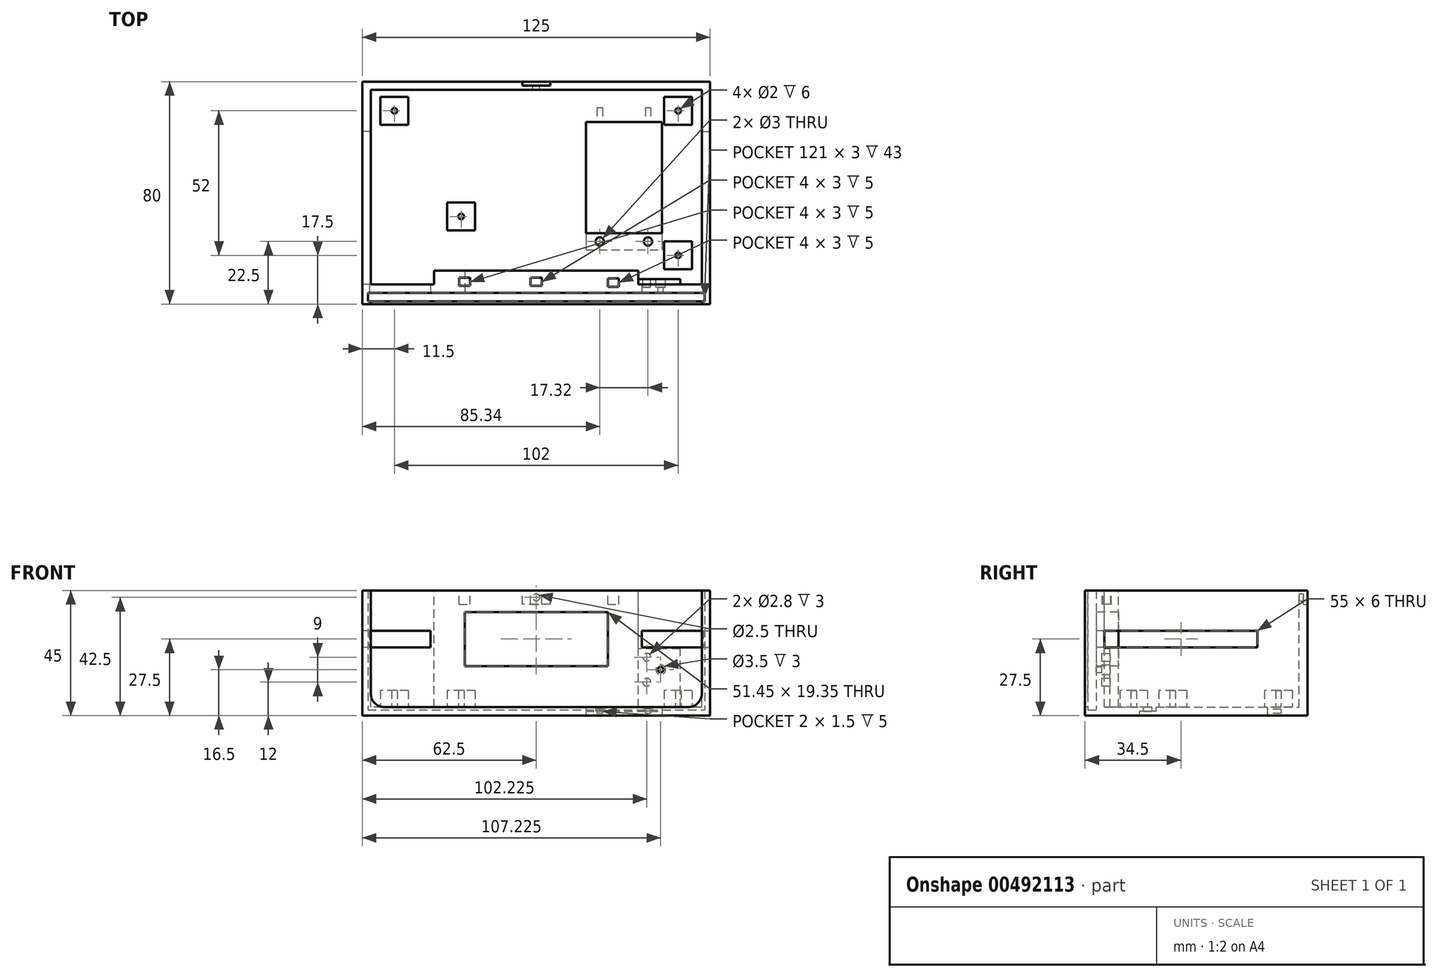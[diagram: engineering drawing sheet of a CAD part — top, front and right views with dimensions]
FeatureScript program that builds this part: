
annotation { "Feature Type Name" : "Feature", "Feature Type Description" : "" }
export const myFeature = defineFeature(function(context is Context, id is Id, definition is map)
    precondition{}
    {
        {
            var Q0;
            Q0=qCreatedBy(makeId("Top.planeOp"),FACE);
            var sketch = newSketch(context, id + "F0", { "sketchPlane" : qUnion([Q0])});
            skLineSegment(sketch, "E0.bottom", {"start": v(-62.5, 40) * mm, "end": v(62.5, 40) * mm});
            skLineSegment(sketch, "E0.top", {"start": v(-62.5, -40) * mm, "end": v(62.5, -40) * mm});
            skLineSegment(sketch, "E0.left", {"start": v(-62.5, 40) * mm, "end": v(-62.5, -40) * mm});
            skLineSegment(sketch, "E0.right", {"start": v(62.5, 40) * mm, "end": v(62.5, -40) * mm});
            skPoint(sketch, "E0.middle", {"position": v(0, 0) * mm});
            skSolve(sketch);
        }
        {
            var Q0;
            Q0 = qSketchRegion(id + "F0", true);
            var Q1;
            Q1 = qSketchRegion(id + "F2", true);
            extrude(context, id + "F1", {"entities" : qUnion([Q0, Q1]), "depth" : 45 * mm});
        }
        {
            var Q0;
            Q0=makeQuery(id+"F1.opExtrude","SWEPT_FACE",FACE,{"disambiguationData":[OSD([sQuery(id+"F0.wireOp",EDGE,"E0.top")])]});
            var sketch = newSketch(context, id + "F2", { "sketchPlane" : qUnion([Q0])});
            skArc(sketch, "E1", {"start": v(-59.5, 7.95) * mm, "mid": v(-58.05, 4.45) * mm, "end": v(-54.55, 3) * mm});
            skLineSegment(sketch, "E2", {"start": v(-59.5, 47) * mm, "end": v(-59.5, 7.95) * mm});
            skLineSegment(sketch, "E3", {"start": v(-54.55, 3) * mm, "end": v(0, 3) * mm});
            skLineSegment(sketch, "E4", {"start": v(0, 47) * mm, "end": v(-59.5, 47) * mm});
            skLineSegment(sketch, "E5.MirrorCS", {"start": v(0, 47) * mm, "end": v(59.5, 47) * mm});
            skLineSegment(sketch, "E6.MirrorCS", {"start": v(59.5, 47) * mm, "end": v(59.5, 7.95) * mm});
            skArc(sketch, "E7.MirrorCS", {"start": v(59.5, 7.95) * mm, "mid": v(58.05, 4.45) * mm, "end": v(54.55, 3) * mm});
            skLineSegment(sketch, "E8.MirrorCS", {"start": v(54.55, 3) * mm, "end": v(0, 3) * mm});
            skSolve(sketch);
        }
        {
            var Q0;
            Q0 = qSketchRegion(id + "F2", true);
            extrude(context, id + "F3", {"entities" : qUnion([Q0]), "operationType" : NewBodyOperationType.REMOVE, "oppositeDirection" : true, "depth" : 4 * mm});
        }
        {
            var Q0;
            Q0=makeQuery(id+"F3.boolean.opBoolean","COPY",FACE,{"derivedFrom":makeQuery(id+"F3.opExtrude","CAP_FACE",FACE,{"disambiguationData":[OSD([sQuery(id+"F2.wireOp",EDGE,"E1"),sQuery(id+"F2.wireOp",EDGE,"E2"),sQuery(id+"F2.wireOp",EDGE,"E3"),sQuery(id+"F2.wireOp",EDGE,"E4"),sQuery(id+"F2.wireOp",EDGE,"3b1f1dae-3a7a-4ead-be68-3ca8e11536510.MirrorCS"),sQuery(id+"F2.wireOp",EDGE,"84f603e4-86f5-4add-9121-f122701d1a8b0.MirrorCS"),sQuery(id+"F2.wireOp",EDGE,"d1928d76-ccfc-4052-b61b-d85eb2371b270.MirrorCS"),sQuery(id+"F2.wireOp",EDGE,"2d53626f-7717-42d7-a231-c828f44102550.MirrorCS")])],"isStart":false})});
            var sketch = newSketch(context, id + "F4", { "sketchPlane" : qUnion([Q0])});
            skLineSegment(sketch, "E9.bottom", {"start": v(-60.5, 48.77) * mm, "end": v(60.5, 48.77) * mm});
            skLineSegment(sketch, "E9.top", {"start": v(-60.5, 2) * mm, "end": v(60.5, 2) * mm});
            skLineSegment(sketch, "E9.left", {"start": v(-60.5, 48.77) * mm, "end": v(-60.5, 2) * mm});
            skLineSegment(sketch, "E9.right", {"start": v(60.5, 48.77) * mm, "end": v(60.5, 2) * mm});
            skSolve(sketch);
        }
        {
            var Q0;
            Q0 = qSketchRegion(id + "F4", true);
            extrude(context, id + "F5", {"entities" : qUnion([Q0]), "operationType" : NewBodyOperationType.REMOVE, "depth" : 3 * mm});
        }
        {
            var Q0;
            Q0=makeQuery(id+"FC8tPhdfjqkrI66_1.boolean.opBoolean","MERGE",FACE,{"derivedFrom":[makeQuery(id+"F3.boolean.opBoolean","COPY",FACE,{"derivedFrom":makeQuery(id+"F3.opExtrude","CAP_FACE",FACE,{"disambiguationData":[OSD([sQuery(id+"F2.wireOp",EDGE,"E1"),sQuery(id+"F2.wireOp",EDGE,"E2"),sQuery(id+"F2.wireOp",EDGE,"E3"),sQuery(id+"F2.wireOp",EDGE,"E4"),sQuery(id+"F2.wireOp",EDGE,"3b1f1dae-3a7a-4ead-be68-3ca8e11536510.MirrorCS"),sQuery(id+"F2.wireOp",EDGE,"84f603e4-86f5-4add-9121-f122701d1a8b0.MirrorCS"),sQuery(id+"F2.wireOp",EDGE,"d1928d76-ccfc-4052-b61b-d85eb2371b270.MirrorCS"),sQuery(id+"F2.wireOp",EDGE,"2d53626f-7717-42d7-a231-c828f44102550.MirrorCS")])],"isStart":false})}),makeQuery(id+"FC8tPhdfjqkrI66_1.opExtrude","CAP_FACE",FACE,{"disambiguationData":[OSD([sQuery(id+"F4.wireOp",EDGE,"35468f4d-d832-4547-b985-8fedb977b133"),sQuery(id+"F4.wireOp",EDGE,"2b2f81fc-e684-446a-be1f-5cde59f2eb81"),sQuery(id+"F4.wireOp",EDGE,"8313b4b1-519a-4c61-ad77-b6e1bf83794d"),sQuery(id+"F4.wireOp",EDGE,"12ae7207-d49d-4211-b3fa-de00408e4e65.MirrorCS"),sQuery(id+"F4.wireOp",EDGE,"1f2af44f-5197-409c-8cd8-adaf810789a4.MirrorCS"),sQuery(id+"F4.wireOp",EDGE,"a53bacdb-3d93-4dea-8849-7c1f9feb08b3.MirrorCS")])],"isStart":true})]});
            var sketch = newSketch(context, id + "F6", { "sketchPlane" : qUnion([Q0])});
            skLineSegment(sketch, "E10.bottom", {"start": v(-25.73, 37.17) * mm, "end": v(25.72, 37.17) * mm});
            skLineSegment(sketch, "E10.top", {"start": v(-25.73, 17.83) * mm, "end": v(25.72, 17.83) * mm});
            skLineSegment(sketch, "E10.left", {"start": v(-25.73, 37.17) * mm, "end": v(-25.73, 17.82) * mm});
            skLineSegment(sketch, "E10.right", {"start": v(25.72, 37.17) * mm, "end": v(25.72, 17.82) * mm});
            skPoint(sketch, "E10.middle", {"position": v(0, 27.5) * mm});
            skLineSegment(sketch, "E11.bottom", {"start": v(-60, 30.5) * mm, "end": v(-38, 30.5) * mm});
            skLineSegment(sketch, "E11.top", {"start": v(-60, 24.5) * mm, "end": v(-38, 24.5) * mm});
            skLineSegment(sketch, "E11.left", {"start": v(-60, 30.5) * mm, "end": v(-60, 24.5) * mm});
            skLineSegment(sketch, "E11.right", {"start": v(-38, 30.5) * mm, "end": v(-38, 24.5) * mm});
            skPoint(sketch, "E11.middle", {"position": v(-49, 27.5) * mm});
            skLineSegment(sketch, "E12.MirrorCS", {"start": v(38, 30.5) * mm, "end": v(38, 24.5) * mm});
            skLineSegment(sketch, "E13.MirrorCS", {"start": v(60, 30.5) * mm, "end": v(38, 30.5) * mm});
            skLineSegment(sketch, "E14.MirrorCS", {"start": v(60, 24.5) * mm, "end": v(38, 24.5) * mm});
            skLineSegment(sketch, "E15.MirrorCS", {"start": v(60, 30.5) * mm, "end": v(60, 24.5) * mm});
            skSolve(sketch);
        }
        {
            var Q0;
            Q0 = qSketchRegion(id + "F6", true);
            extrude(context, id + "F7", {"entities" : qUnion([Q0]), "operationType" : NewBodyOperationType.REMOVE, "oppositeDirection" : true, "depth" : 50 * mm});
        }
        {
            var Q0;
            Q0=makeQuery(id+"F1.opExtrude","CAP_FACE",FACE,{"disambiguationData":[OSD([sQuery(id+"F0.wireOp",EDGE,"E0.bottom"),sQuery(id+"F0.wireOp",EDGE,"E0.top"),sQuery(id+"F0.wireOp",EDGE,"E0.left"),sQuery(id+"F0.wireOp",EDGE,"E0.right")])],"isStart":false});
            var sketch = newSketch(context, id + "F8", { "sketchPlane" : qUnion([Q0])});
            skLineSegment(sketch, "E16", {"start": v(0, -28) * mm, "end": v(-36.72, -28) * mm});
            skLineSegment(sketch, "E17", {"start": v(-36.73, -28) * mm, "end": v(-36.73, -33) * mm});
            skLineSegment(sketch, "E18", {"start": v(-36.73, -33) * mm, "end": v(-59.5, -33) * mm});
            skLineSegment(sketch, "E19", {"start": v(-59.5, -33) * mm, "end": v(-59.5, 37) * mm});
            skLineSegment(sketch, "E20", {"start": v(0, -28) * mm, "end": v(0, 37) * mm});
            skPoint(sketch, "E20.endSnap0", {"position": v(0, 40) * mm});
            skLineSegment(sketch, "E21", {"start": v(0, 37) * mm, "end": v(-59.5, 37) * mm});
            skLineSegment(sketch, "E22.MirrorCS", {"start": v(0, 37) * mm, "end": v(59.5, 37) * mm});
            skLineSegment(sketch, "E23.MirrorCS", {"start": v(59.5, -33) * mm, "end": v(59.5, 37) * mm});
            skLineSegment(sketch, "E24.MirrorCS", {"start": v(36.73, -33) * mm, "end": v(59.5, -33) * mm});
            skLineSegment(sketch, "E25.MirrorCS", {"start": v(36.73, -28) * mm, "end": v(36.73, -33) * mm});
            skLineSegment(sketch, "E26.MirrorCS", {"start": v(0, -28) * mm, "end": v(36.72, -28) * mm});
            skSolve(sketch);
        }
        {
            var Q0;
            Q0 = qSketchRegion(id + "F8", true);
            extrude(context, id + "F9", {"entities" : qUnion([Q0]), "operationType" : NewBodyOperationType.REMOVE, "oppositeDirection" : true, "depth" : (45 - 3) * mm});
        }
        {
            var Q0;
            Q0=makeQuery(id+"F9.boolean.opBoolean","COPY",FACE,{"derivedFrom":makeQuery(id+"F9.opExtrude","CAP_FACE",FACE,{"disambiguationData":[OSD([sQuery(id+"F8.wireOp",EDGE,"E16"),sQuery(id+"F8.wireOp",EDGE,"E17"),sQuery(id+"F8.wireOp",EDGE,"E18"),sQuery(id+"F8.wireOp",EDGE,"E19"),sQuery(id+"F8.wireOp",EDGE,"E21"),sQuery(id+"F8.wireOp",EDGE,"E22.MirrorCS"),sQuery(id+"F8.wireOp",EDGE,"E23.MirrorCS"),sQuery(id+"F8.wireOp",EDGE,"E24.MirrorCS"),sQuery(id+"F8.wireOp",EDGE,"E25.MirrorCS"),sQuery(id+"F8.wireOp",EDGE,"E26.MirrorCS")])],"isStart":false})});
            var sketch = newSketch(context, id + "F10", { "sketchPlane" : qUnion([Q0])});
            skLineSegment(sketch, "E27.bottom", {"start": v(-46, 34.5) * mm, "end": v(-56, 34.5) * mm});
            skLineSegment(sketch, "E27.top", {"start": v(-46, 24.5) * mm, "end": v(-56, 24.5) * mm});
            skLineSegment(sketch, "E27.left", {"start": v(-46, 34.5) * mm, "end": v(-46, 24.5) * mm});
            skLineSegment(sketch, "E27.right", {"start": v(-56, 34.5) * mm, "end": v(-56, 24.5) * mm});
            skPoint(sketch, "E27.middle", {"position": v(-51, 29.5) * mm});
            skLineSegment(sketch, "E28.bottom", {"start": v(56, 34.5) * mm, "end": v(46, 34.5) * mm});
            skLineSegment(sketch, "E28.top", {"start": v(56, 24.5) * mm, "end": v(46, 24.5) * mm});
            skLineSegment(sketch, "E28.left", {"start": v(56, 34.5) * mm, "end": v(56, 24.5) * mm});
            skLineSegment(sketch, "E28.right", {"start": v(46, 34.5) * mm, "end": v(46, 24.5) * mm});
            skPoint(sketch, "E28.middle", {"position": v(51, 29.5) * mm});
            skLineSegment(sketch, "E29.bottom", {"start": v(56, -17.5) * mm, "end": v(46, -17.5) * mm});
            skLineSegment(sketch, "E29.top", {"start": v(56, -27.5) * mm, "end": v(46, -27.5) * mm});
            skLineSegment(sketch, "E29.left", {"start": v(56, -17.5) * mm, "end": v(56, -27.5) * mm});
            skLineSegment(sketch, "E29.right", {"start": v(46, -17.5) * mm, "end": v(46, -27.5) * mm});
            skPoint(sketch, "E29.middle", {"position": v(51, -22.5) * mm});
            skLineSegment(sketch, "E30.bottom", {"start": v(-22, -3.5) * mm, "end": v(-32, -3.5) * mm});
            skLineSegment(sketch, "E30.top", {"start": v(-22, -13.5) * mm, "end": v(-32, -13.5) * mm});
            skLineSegment(sketch, "E30.left", {"start": v(-22, -3.5) * mm, "end": v(-22, -13.5) * mm});
            skLineSegment(sketch, "E30.right", {"start": v(-32, -3.5) * mm, "end": v(-32, -13.5) * mm});
            skPoint(sketch, "E30.middle", {"position": v(-27, -8.5) * mm});
            skCircle(sketch, "E31", {"center": v(-51, 29.5) * mm, "radius": 1 * mm});
            skCircle(sketch, "E32", {"center": v(51, 29.5) * mm, "radius": 1 * mm});
            skCircle(sketch, "E33", {"center": v(51, -22.5) * mm, "radius": 1 * mm});
            skCircle(sketch, "E34", {"center": v(-27, -8.5) * mm, "radius": 1 * mm});
            skSolve(sketch);
        }
        {
            var Q0;
            Q0 = qSketchRegion(id + "F10", true);
            extrude(context, id + "F11", {"entities" : qUnion([Q0]), "operationType" : NewBodyOperationType.ADD, "depth" : 6 * mm});
        }
        {
            var Q0;
            Q0=makeQuery(id+"F1.opExtrude","SWEPT_FACE",FACE,{"disambiguationData":[OSD([sQuery(id+"F0.wireOp",EDGE,"E0.left")])]});
            var sketch = newSketch(context, id + "F12", { "sketchPlane" : qUnion([Q0])});
            skLineSegment(sketch, "E35.bottom", {"start": v(-22, 30.5) * mm, "end": v(33, 30.5) * mm});
            skLineSegment(sketch, "E35.top", {"start": v(-22, 24.5) * mm, "end": v(33, 24.5) * mm});
            skLineSegment(sketch, "E35.left", {"start": v(-22, 30.5) * mm, "end": v(-22, 24.5) * mm});
            skLineSegment(sketch, "E35.right", {"start": v(33, 30.5) * mm, "end": v(33, 24.5) * mm});
            skPoint(sketch, "E35.middle", {"position": v(5.5, 27.5) * mm});
            skSolve(sketch);
        }
        {
            var Q0;
            Q0 = qSketchRegion(id + "F12", true);
            extrude(context, id + "F13", {"entities" : qUnion([Q0]), "operationType" : NewBodyOperationType.REMOVE, "oppositeDirection" : true, "depth" : 10 * mm});
        }
        {
            var Q0;
            Q0=makeQuery(id+"F1.opExtrude","SWEPT_FACE",FACE,{"disambiguationData":[OSD([sQuery(id+"F0.wireOp",EDGE,"E0.right")])]});
            var sketch = newSketch(context, id + "F14", { "sketchPlane" : qUnion([Q0])});
            skLineSegment(sketch, "E36.bottom", {"start": v(-33, 30.5) * mm, "end": v(22, 30.5) * mm});
            skLineSegment(sketch, "E36.top", {"start": v(-33, 24.5) * mm, "end": v(22, 24.5) * mm});
            skLineSegment(sketch, "E36.left", {"start": v(-33, 30.5) * mm, "end": v(-33, 24.5) * mm});
            skLineSegment(sketch, "E36.right", {"start": v(22, 30.5) * mm, "end": v(22, 24.5) * mm});
            skPoint(sketch, "E36.middle", {"position": v(-5.5, 27.5) * mm});
            skSolve(sketch);
        }
        {
            var Q0;
            Q0 = qSketchRegion(id + "F14", true);
            extrude(context, id + "F15", {"entities" : qUnion([Q0]), "operationType" : NewBodyOperationType.REMOVE, "oppositeDirection" : true, "depth" : 10 * mm});
        }
        {
            var Q0;
            Q0=makeQuery(id+"F0.imprint","IMPRINT",FACE,{"disambiguationData":[TD([[makeQuery(id+"F0.imprint","IMPRINT",EDGE,{"derivedFrom":sQuery(id+"F0.wireOp",EDGE,"E0.bottom")}),-1.0]])]});
            var sketch = newSketch(context, id + "F16", { "sketchPlane" : qUnion([Q0])});
            skLineSegment(sketch, "E37.bottom", {"start": v(45.16, 25.5) * mm, "end": v(17.84, 25.5) * mm});
            skLineSegment(sketch, "E37.top", {"start": v(45.16, -14.5) * mm, "end": v(17.84, -14.5) * mm});
            skLineSegment(sketch, "E37.left", {"start": v(45.16, 25.5) * mm, "end": v(45.16, -14.5) * mm});
            skLineSegment(sketch, "E37.right", {"start": v(17.84, 25.5) * mm, "end": v(17.84, -14.5) * mm});
            skPoint(sketch, "E37.middle", {"position": v(31.5, 5.5) * mm});
            skSolve(sketch);
        }
        {
            var Q0;
            Q0 = qSketchRegion(id + "F16", true);
            extrude(context, id + "F17", {"entities" : qUnion([Q0]), "operationType" : NewBodyOperationType.REMOVE, "depth" : 25 * mm});
        }
        {
            var Q0;
            Q0=makeQuery(id+"F1.opExtrude","SWEPT_FACE",FACE,{"disambiguationData":[OSD([sQuery(id+"F0.wireOp",EDGE,"E0.bottom")])]});
            cPlane(context, id + "F18", {"entities" : qUnion([Q0]), "cplaneType" : CPlaneType.OFFSET, "offset" : 14.5 * mm, "oppositeDirection" : true, "width" : 150 * mm, "height" : 150 * mm});
        }
        {
            var Q0;
            Q0=qCreatedBy(id+"F18.planeOp",FACE);
            var sketch = newSketch(context, id + "F19", { "sketchPlane" : qUnion([Q0])});
            skLineSegment(sketch, "E38.bottom", {"start": v(-23.84, 2.25) * mm, "end": v(-21.84, 2.25) * mm});
            skLineSegment(sketch, "E38.top", {"start": v(-23.84, 0.75) * mm, "end": v(-21.84, 0.75) * mm});
            skLineSegment(sketch, "E38.left", {"start": v(-23.84, 2.25) * mm, "end": v(-23.84, 0.75) * mm});
            skLineSegment(sketch, "E38.right", {"start": v(-21.84, 2.25) * mm, "end": v(-21.84, 0.75) * mm});
            skPoint(sketch, "E38.middle", {"position": v(-22.84, 1.5) * mm});
            skLineSegment(sketch, "E39.bottom", {"start": v(-41.16, 2.25) * mm, "end": v(-39.16, 2.25) * mm});
            skLineSegment(sketch, "E39.top", {"start": v(-41.16, 0.75) * mm, "end": v(-39.16, 0.75) * mm});
            skLineSegment(sketch, "E39.left", {"start": v(-41.16, 2.25) * mm, "end": v(-41.16, 0.75) * mm});
            skLineSegment(sketch, "E39.right", {"start": v(-39.16, 2.25) * mm, "end": v(-39.16, 0.75) * mm});
            skPoint(sketch, "E39.middle", {"position": v(-40.16, 1.5) * mm});
            skSolve(sketch);
        }
        {
            var Q0;
            Q0 = qSketchRegion(id + "F19", true);
            extrude(context, id + "F20", {"entities" : qUnion([Q0]), "operationType" : NewBodyOperationType.REMOVE, "depth" : 5 * mm});
        }
        {
            var Q0;
            Q0=makeQuery(id+"F0.imprint","IMPRINT",FACE,{"disambiguationData":[TD([[makeQuery(id+"F0.imprint","IMPRINT",EDGE,{"derivedFrom":sQuery(id+"F0.wireOp",EDGE,"E0.bottom")}),-1.0]])]});
            var sketch = newSketch(context, id + "F21", { "sketchPlane" : qUnion([Q0])});
            skLineSegment(sketch, "E40.bottom", {"start": v(17.84, -14.5) * mm, "end": v(45.16, -14.5) * mm});
            skLineSegment(sketch, "E40.top", {"start": v(17.84, -20.5) * mm, "end": v(45.16, -20.5) * mm});
            skLineSegment(sketch, "E40.left", {"start": v(17.84, -14.5) * mm, "end": v(17.84, -20.5) * mm});
            skLineSegment(sketch, "E40.right", {"start": v(45.16, -14.5) * mm, "end": v(45.16, -20.5) * mm});
            skSolve(sketch);
        }
        {
            var Q0;
            Q0 = qSketchRegion(id + "F21", true);
            extrude(context, id + "F22", {"entities" : qUnion([Q0]), "operationType" : NewBodyOperationType.REMOVE, "depth" : 1.5 * mm});
        }
        {
            var Q0;
            Q0=makeQuery(id+"F16.imprint","IMPRINT",FACE,{"disambiguationData":[TD([[makeQuery(id+"F16.imprint","IMPRINT",EDGE,{"derivedFrom":sQuery(id+"F16.wireOp",EDGE,"E37.bottom")}),-1.0]])]});
            cPlane(context, id + "F23", {"entities" : qUnion([Q0]), "cplaneType" : CPlaneType.OFFSET, "offset" : 1.5 * mm, "width" : 150 * mm, "height" : 150 * mm});
        }
        {
            var Q0;
            Q0=qCreatedBy(id+"F23.planeOp",FACE);
            var sketch = newSketch(context, id + "F24", { "sketchPlane" : qUnion([Q0])});
            skCircle(sketch, "E41", {"center": v(22.84, -17.5) * mm, "radius": 1.5 * mm});
            skCircle(sketch, "E42", {"center": v(40.16, -17.5) * mm, "radius": 1.5 * mm});
            skSolve(sketch);
        }
        {
            var Q0;
            Q0 = qSketchRegion(id + "F24", true);
            extrude(context, id + "F25", {"entities" : qUnion([Q0]), "operationType" : NewBodyOperationType.REMOVE, "depth" : 10 * mm});
        }
        {
            var Q0;
            Q0=makeQuery(id+"F8.imprint","IMPRINT",FACE,{"disambiguationData":[TD([[makeQuery(id+"F8.imprint","IMPRINT",EDGE,{"derivedFrom":sQuery(id+"F8.wireOp",EDGE,"E16")}),1.0]])]});
            var sketch = newSketch(context, id + "F26", { "sketchPlane" : qUnion([Q0])});
            skLineSegment(sketch, "E43.bottom", {"start": v(-2, -30.5) * mm, "end": v(2, -30.5) * mm});
            skLineSegment(sketch, "E43.top", {"start": v(-2, -33.5) * mm, "end": v(2, -33.5) * mm});
            skLineSegment(sketch, "E43.left", {"start": v(-2, -30.5) * mm, "end": v(-2, -33.5) * mm});
            skLineSegment(sketch, "E43.right", {"start": v(2, -30.5) * mm, "end": v(2, -33.5) * mm});
            skPoint(sketch, "E43.middle", {"position": v(0, -32) * mm});
            skLineSegment(sketch, "E44.bottom", {"start": v(-27.73, -30.5) * mm, "end": v(-23.72, -30.5) * mm});
            skLineSegment(sketch, "E44.top", {"start": v(-27.73, -33.5) * mm, "end": v(-23.72, -33.5) * mm});
            skLineSegment(sketch, "E44.left", {"start": v(-27.73, -30.5) * mm, "end": v(-27.73, -33.5) * mm});
            skLineSegment(sketch, "E44.right", {"start": v(-23.72, -30.5) * mm, "end": v(-23.72, -33.5) * mm});
            skPoint(sketch, "E44.middle", {"position": v(-25.72, -32) * mm});
            skLineSegment(sketch, "E45.bottom", {"start": v(25.73, -30.77) * mm, "end": v(29.73, -30.77) * mm});
            skLineSegment(sketch, "E45.top", {"start": v(25.73, -33.77) * mm, "end": v(29.73, -33.77) * mm});
            skLineSegment(sketch, "E45.left", {"start": v(25.73, -30.77) * mm, "end": v(25.73, -33.77) * mm});
            skLineSegment(sketch, "E45.right", {"start": v(29.73, -30.77) * mm, "end": v(29.73, -33.77) * mm});
            skPoint(sketch, "E45.middle", {"position": v(27.73, -32.27) * mm});
            skSolve(sketch);
        }
        {
            var Q0;
            Q0 = qSketchRegion(id + "F26", true);
            extrude(context, id + "F27", {"entities" : qUnion([Q0]), "operationType" : NewBodyOperationType.REMOVE, "oppositeDirection" : true, "depth" : 5 * mm});
        }
        {
            var Q0;
            Q0=makeQuery(id+"F1.opExtrude","SWEPT_FACE",FACE,{"disambiguationData":[OSD([sQuery(id+"F0.wireOp",EDGE,"E0.bottom")])]});
            var sketch = newSketch(context, id + "F28", { "sketchPlane" : qUnion([Q0])});
            skLineSegment(sketch, "E46.bottom", {"start": v(-5, 40) * mm, "end": v(5, 40) * mm});
            skLineSegment(sketch, "E46.top", {"start": v(-5, 50) * mm, "end": v(5, 50) * mm});
            skLineSegment(sketch, "E46.left", {"start": v(-5, 40) * mm, "end": v(-5, 50) * mm});
            skLineSegment(sketch, "E46.right", {"start": v(5, 40) * mm, "end": v(5, 50) * mm});
            skPoint(sketch, "E46.middle", {"position": v(0, 45) * mm});
            skSolve(sketch);
        }
        {
            var Q0;
            Q0 = qSketchRegion(id + "F28", true);
            extrude(context, id + "F29", {"entities" : qUnion([Q0]), "operationType" : NewBodyOperationType.REMOVE, "oppositeDirection" : true, "depth" : 1.5 * mm});
        }
        {
            var Q0;
            Q0=makeQuery(id+"F29.boolean.opBoolean","COPY",FACE,{"derivedFrom":makeQuery(id+"F29.opExtrude","CAP_FACE",FACE,{"disambiguationData":[OSD([sQuery(id+"F28.wireOp",EDGE,"E46.bottom"),sQuery(id+"F28.wireOp",EDGE,"E46.top"),sQuery(id+"F28.wireOp",EDGE,"E46.left"),sQuery(id+"F28.wireOp",EDGE,"E46.right")])],"isStart":false})});
            var sketch = newSketch(context, id + "F30", { "sketchPlane" : qUnion([Q0])});
            skCircle(sketch, "E47", {"center": v(0, 42.5) * mm, "radius": 1.25 * mm});
            skSolve(sketch);
        }
        {
            var Q0;
            Q0 = qSketchRegion(id + "F30", true);
            extrude(context, id + "F31", {"entities" : qUnion([Q0]), "operationType" : NewBodyOperationType.REMOVE, "oppositeDirection" : true, "depth" : 10 * mm});
        }
        {
            var Q0;
            Q0=makeQuery(id+"F9.boolean.opBoolean","COPY",FACE,{"derivedFrom":makeQuery(id+"F9.opExtrude","SWEPT_FACE",FACE,{"disambiguationData":[OSD([sQuery(id+"F8.wireOp",EDGE,"E24.MirrorCS")])]})});
            var sketch = newSketch(context, id + "F32", { "sketchPlane" : qUnion([Q0])});
            skLineSegment(sketch, "E48", {"start": v(-51.72, 3) * mm, "end": v(-51.72, 24) * mm});
            skLineSegment(sketch, "E49", {"start": v(-51.72, 24) * mm, "end": v(-36.72, 24) * mm});
            skLineSegment(sketch, "E50", {"start": v(-36.72, 24) * mm, "end": v(-36.72, 3) * mm});
            skLineSegment(sketch, "E51", {"start": v(-36.72, 3) * mm, "end": v(-51.72, 3) * mm});
            skSolve(sketch);
        }
        {
            var Q0;
            Q0 = qSketchRegion(id + "F32", true);
            var Q1;
            Q1 = qSketchRegion(id + "F34", true);
            extrude(context, id + "F33", {"entities" : qUnion([Q0, Q1]), "operationType" : NewBodyOperationType.ADD, "depth" : 2 * mm});
        }
        {
            var Q0;
            Q0=makeQuery(id+"F33.opExtrude","CAP_FACE",FACE,{"disambiguationData":[OSD([sQuery(id+"F32.wireOp",EDGE,"E48"),sQuery(id+"F32.wireOp",EDGE,"E49"),sQuery(id+"F32.wireOp",EDGE,"E50"),sQuery(id+"F32.wireOp",EDGE,"E51")])],"isStart":false});
            var sketch = newSketch(context, id + "F34", { "sketchPlane" : qUnion([Q0])});
            skCircle(sketch, "E52", {"center": v(-39.72, 21) * mm, "radius": 1.4 * mm});
            skCircle(sketch, "E53", {"center": v(-39.72, 12) * mm, "radius": 1.4 * mm});
            skCircle(sketch, "E54", {"center": v(-44.72, 16.5) * mm, "radius": 1.75 * mm});
            skSolve(sketch);
        }
        {
            var Q0;
            Q0 = qSketchRegion(id + "F34", true);
            extrude(context, id + "F35", {"entities" : qUnion([Q0]), "operationType" : NewBodyOperationType.REMOVE, "oppositeDirection" : true, "depth" : 3 * mm});
        }
        {
            var Q0;
            Q0=makeQuery(id+"F35.boolean.opBoolean","COPY",FACE,{"derivedFrom":makeQuery(id+"F35.opExtrude","CAP_FACE",FACE,{"disambiguationData":[OSD([sQuery(id+"F34.wireOp",EDGE,"E54")])],"isStart":false})});
            var sketch = newSketch(context, id + "F36", { "sketchPlane" : qUnion([Q0])});
            skCircle(sketch, "E55", {"center": v(-44.72, 16.5) * mm, "radius": 1 * mm});
            skSolve(sketch);
        }
        {
            var Q0;
            Q0 = qSketchRegion(id + "F36", true);
            extrude(context, id + "F37", {"entities" : qUnion([Q0]), "operationType" : NewBodyOperationType.REMOVE, "oppositeDirection" : true, "depth" : 25 * mm});
        }
    });
